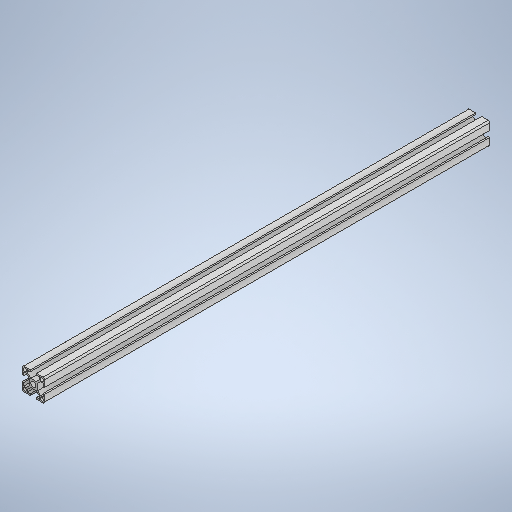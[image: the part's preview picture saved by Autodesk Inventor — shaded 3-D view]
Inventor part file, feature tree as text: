
AUTODESK INVENTOR PART (.ipt)
format: ipt  version: 2025 (Build 290162000, 162)  size: 314,368 bytes
history: native  units: in
note: dims shown in document units (in); Inventor stores cm internally (conversion verified against a paired STEP export)
features: extrude x1, sketch x1
ambient origin geometry x8: Origin, YZ Plane, XZ Plane, XY Plane, X Axis, Y Axis, Z Axis, Center Point
bodies: Solid1 (feature_tree)
feature tree (2):
  extrude  "Extrusion1"  Depth=23.622in
  sketch  "Sketch1"  dims[d6=23.622in d7=0.0in d8=0.1969in d9=0.0344in]
